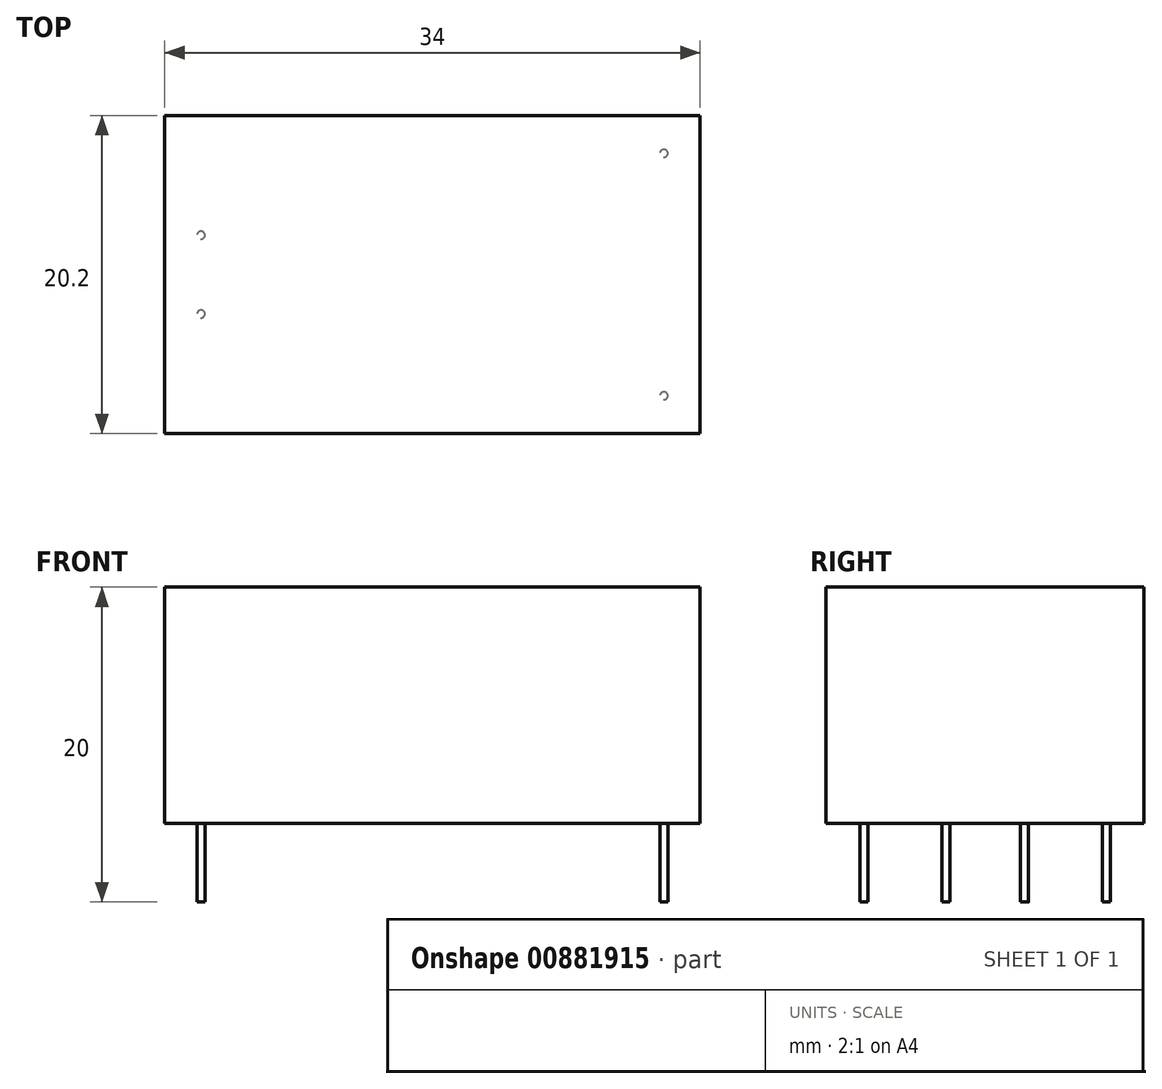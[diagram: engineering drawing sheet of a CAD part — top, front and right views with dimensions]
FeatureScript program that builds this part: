
annotation { "Feature Type Name" : "Feature", "Feature Type Description" : "" }
export const myFeature = defineFeature(function(context is Context, id is Id, definition is map)
    precondition{}
    {
        {
            var Q0;
            Q0=qCreatedBy(makeId("Top.planeOp"),FACE);
            var sketch = newSketch(context, id + "F0", { "sketchPlane" : qUnion([Q0])});
            skLineSegment(sketch, "E0.bottom", {"start": v(17, -10.1) * mm, "end": v(-17, -10.1) * mm});
            skLineSegment(sketch, "E0.top", {"start": v(17, 10.1) * mm, "end": v(-17, 10.1) * mm});
            skLineSegment(sketch, "E0.left", {"start": v(17, -10.1) * mm, "end": v(17, 10.1) * mm});
            skLineSegment(sketch, "E0.right", {"start": v(-17, -10.1) * mm, "end": v(-17, 10.1) * mm});
            skPoint(sketch, "E0.middle", {"position": v(0, 0) * mm});
            skCircle(sketch, "E1", {"center": v(-14.7, 2.5) * mm, "radius": 0.25 * mm});
            skCircle(sketch, "E2", {"center": v(-14.7, -2.5) * mm, "radius": 0.25 * mm});
            skCircle(sketch, "E3", {"center": v(14.7, 7.7) * mm, "radius": 0.25 * mm});
            skCircle(sketch, "E4", {"center": v(14.7, -7.7) * mm, "radius": 0.25 * mm});
            skLineSegment(sketch, "E5", {"start": v(-14.7, 2.5) * mm, "end": v(-14.7, -2.5) * mm, "construction": true});
            skLineSegment(sketch, "E6", {"start": v(14.7, 7.7) * mm, "end": v(14.7, -7.7) * mm, "construction": true});
            skPoint(sketch, "E7", {"position": v(-14.7, 0) * mm});
            skPoint(sketch, "E8", {"position": v(14.7, 0) * mm});
            skLineSegment(sketch, "E9", {"start": v(-14.7, 0) * mm, "end": v(14.7, 0) * mm, "construction": true});
            skSolve(sketch);
        }
        {
            var Q0;
            Q0=makeQuery(id+"F0.imprint","IMPRINT",FACE,{"disambiguationData":[TD([[makeQuery(id+"F0.imprint","IMPRINT",EDGE,{"derivedFrom":sQuery(id+"F0.wireOp",EDGE,"E0.bottom")}),-1.0]])]});
            var Q1;
            Q1=makeQuery(id+"F0.imprint","IMPRINT",FACE,{"disambiguationData":[TD([[makeQuery(id+"F0.imprint","IMPRINT",EDGE,{"derivedFrom":sQuery(id+"F0.wireOp",EDGE,"E3")}),1.0]])]});
            var Q2;
            Q2=makeQuery(id+"F0.imprint","IMPRINT",FACE,{"disambiguationData":[TD([[makeQuery(id+"F0.imprint","IMPRINT",EDGE,{"derivedFrom":sQuery(id+"F0.wireOp",EDGE,"E2")}),1.0]])]});
            var Q3;
            Q3=makeQuery(id+"F0.imprint","IMPRINT",FACE,{"disambiguationData":[TD([[makeQuery(id+"F0.imprint","IMPRINT",EDGE,{"derivedFrom":sQuery(id+"F0.wireOp",EDGE,"E1")}),1.0]])]});
            var Q4;
            Q4=makeQuery(id+"F0.imprint","IMPRINT",FACE,{"disambiguationData":[TD([[makeQuery(id+"F0.imprint","IMPRINT",EDGE,{"derivedFrom":sQuery(id+"F0.wireOp",EDGE,"E4")}),1.0]])]});
            extrude(context, id + "F1", {"entities" : qUnion([Q0, Q1, Q2, Q3, Q4]), "depth" : 15 * mm, "offsetDistance" : 25 * mm});
        }
        {
            var Q0;
            Q0=makeQuery(id+"F0.imprint","IMPRINT",FACE,{"disambiguationData":[TD([[makeQuery(id+"F0.imprint","IMPRINT",EDGE,{"derivedFrom":sQuery(id+"F0.wireOp",EDGE,"E3")}),1.0]])]});
            var Q1;
            Q1=makeQuery(id+"F0.imprint","IMPRINT",FACE,{"disambiguationData":[TD([[makeQuery(id+"F0.imprint","IMPRINT",EDGE,{"derivedFrom":sQuery(id+"F0.wireOp",EDGE,"E2")}),1.0]])]});
            var Q2;
            Q2=makeQuery(id+"F0.imprint","IMPRINT",FACE,{"disambiguationData":[TD([[makeQuery(id+"F0.imprint","IMPRINT",EDGE,{"derivedFrom":sQuery(id+"F0.wireOp",EDGE,"E1")}),1.0]])]});
            var Q3;
            Q3=makeQuery(id+"F0.imprint","IMPRINT",FACE,{"disambiguationData":[TD([[makeQuery(id+"F0.imprint","IMPRINT",EDGE,{"derivedFrom":sQuery(id+"F0.wireOp",EDGE,"E4")}),1.0]])]});
            extrude(context, id + "F2", {"entities" : qUnion([Q0, Q1, Q2, Q3]), "operationType" : NewBodyOperationType.ADD, "oppositeDirection" : true, "depth" : 5 * mm, "offsetDistance" : 25 * mm});
        }
    });
